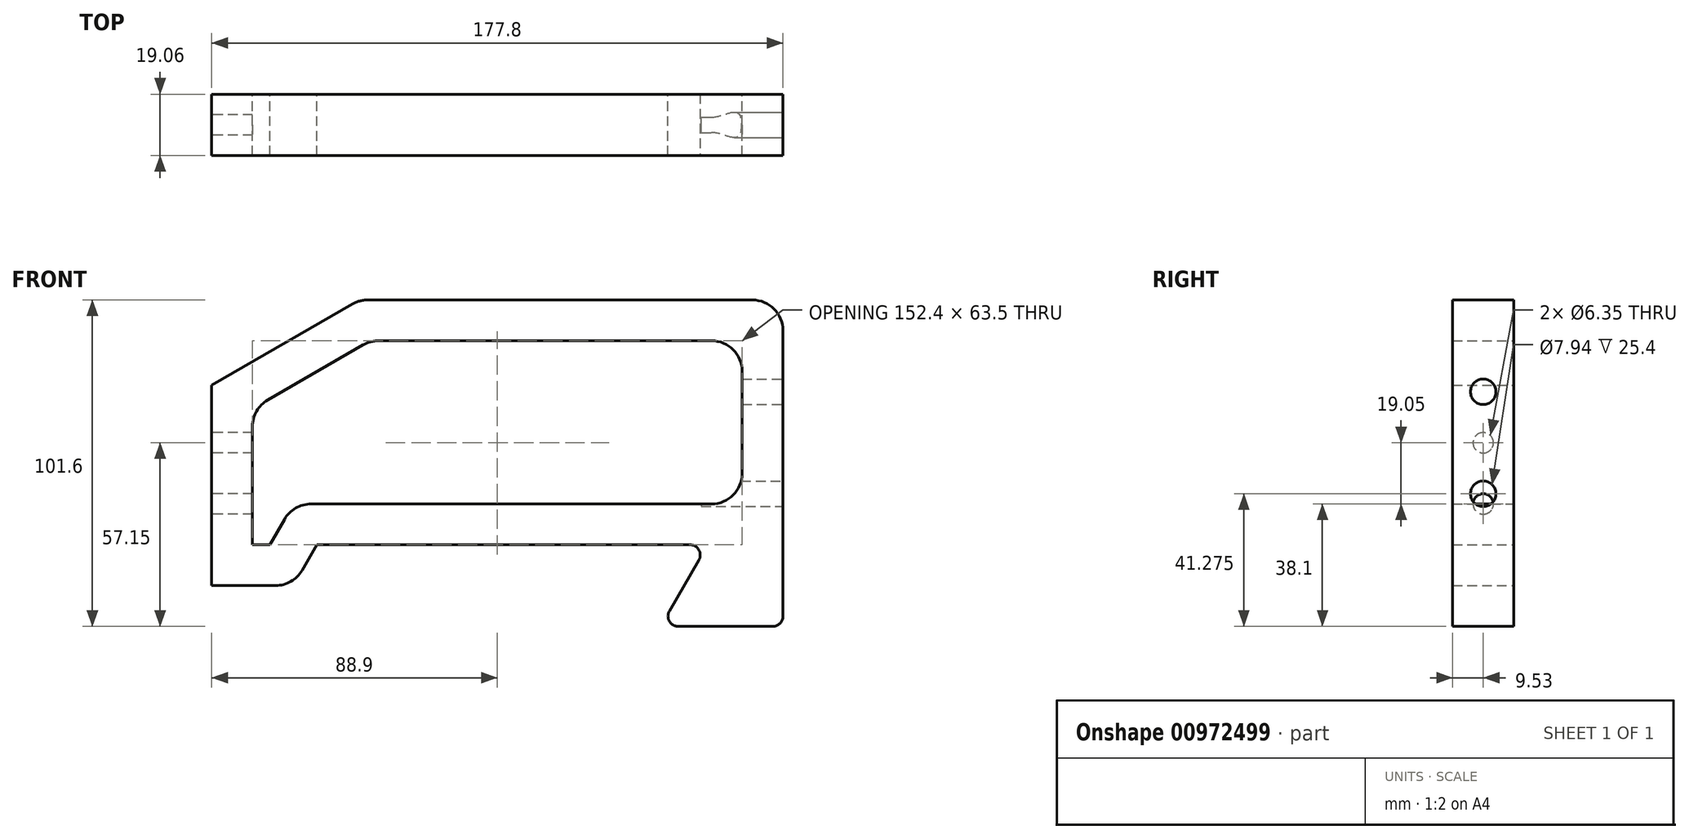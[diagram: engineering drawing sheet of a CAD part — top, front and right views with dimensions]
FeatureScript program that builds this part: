
annotation { "Feature Type Name" : "Feature", "Feature Type Description" : "" }
export const myFeature = defineFeature(function(context is Context, id is Id, definition is map)
    precondition{}
    {
        {
            var Q0;
            Q0=qCreatedBy(makeId("Front.planeOp"),FACE);
            var sketch = newSketch(context, id + "F0", { "sketchPlane" : qUnion([Q0])});
            skLineSegment(sketch, "E0", {"start": v(0, 41.2) * mm, "end": v(0, -82.16) * mm, "construction": true});
            skLineSegment(sketch, "E1", {"start": v(-50.32, 0) * mm, "end": v(100.51, 0) * mm, "construction": true});
            skLineSegment(sketch, "E2", {"start": v(-88.9, 24.27) * mm, "end": v(-88.9, -38.1) * mm});
            skLineSegment(sketch, "E3", {"start": v(-88.9, -38.1) * mm, "end": v(-63.5, -38.1) * mm});
            skLineSegment(sketch, "E4", {"start": v(-63.5, -38.1) * mm, "end": v(-56.17, -25.4) * mm});
            skLineSegment(sketch, "E5", {"start": v(-56.17, -25.4) * mm, "end": v(65.46, -25.4) * mm});
            skLineSegment(sketch, "E6", {"start": v(65.46, -25.4) * mm, "end": v(50.8, -50.8) * mm});
            skLineSegment(sketch, "E7", {"start": v(50.8, -50.8) * mm, "end": v(88.9, -50.8) * mm});
            skLineSegment(sketch, "E8", {"start": v(88.9, -50.8) * mm, "end": v(88.9, 50.8) * mm});
            skLineSegment(sketch, "E9", {"start": v(88.9, 50.8) * mm, "end": v(-42.95, 50.8) * mm});
            skLineSegment(sketch, "E10", {"start": v(-42.95, 50.8) * mm, "end": v(-88.9, 24.27) * mm});
            skLineSegment(sketch, "E11.0", {"start": v(76.2, 38.1) * mm, "end": v(-39.55, 38.1) * mm});
            skLineSegment(sketch, "E11.2", {"start": v(-39.55, 38.1) * mm, "end": v(-76.2, 16.94) * mm});
            skLineSegment(sketch, "E11.5", {"start": v(-76.2, 16.94) * mm, "end": v(-76.2, -25.4) * mm});
            skLineSegment(sketch, "E11.6", {"start": v(-76.2, -25.4) * mm, "end": v(-70.83, -25.4) * mm});
            skLineSegment(sketch, "E11.7", {"start": v(-70.83, -25.4) * mm, "end": v(-63.5, -12.7) * mm});
            skLineSegment(sketch, "E11.8", {"start": v(-63.5, -12.7) * mm, "end": v(76.2, -12.7) * mm});
            skLineSegment(sketch, "E12.trimOffspring", {"start": v(76.2, -12.7) * mm, "end": v(76.2, 38.1) * mm});
            skSolve(sketch);
        }
        {
            var Q0;
            Q0=makeQuery(id+"F0.imprint","IMPRINT",FACE,{"disambiguationData":[TD([[makeQuery(id+"F0.imprint","IMPRINT",EDGE,{"derivedFrom":sQuery(id+"F0.wireOp",EDGE,"E2")}),1.0]])]});
            extrude(context, id + "F1", {"entities" : qUnion([Q0]), "depth" : 9.52 * mm, "offsetDistance" : 25.4 * mm, "hasSecondDirection" : true, "secondDirectionOppositeDirection" : true, "secondDirectionDepth" : 9.52 * mm});
        }
        {
            var Q0;
            Q0=makeQuery(id+"F1.opExtrude","SWEPT_EDGE",EDGE,{"disambiguationData":[OSD([sQuery(id+"F0.wireOp",EDGE,"E8"),sQuery(id+"F0.wireOp",EDGE,"E9")])]});
            var Q1;
            Q1=makeQuery(id+"F1.opExtrude","SWEPT_EDGE",EDGE,{"disambiguationData":[OSD([sQuery(id+"F0.wireOp",EDGE,"E9"),sQuery(id+"F0.wireOp",EDGE,"E10")])]});
            var Q2;
            Q2=makeQuery(id+"F1.opExtrude","SWEPT_EDGE",EDGE,{"disambiguationData":[OSD([sQuery(id+"F0.wireOp",EDGE,"E3"),sQuery(id+"F0.wireOp",EDGE,"E4")])]});
            var Q3;
            Q3=makeQuery(id+"F1.opExtrude","SWEPT_EDGE",EDGE,{"disambiguationData":[OSD([sQuery(id+"F0.wireOp",EDGE,"E11.2"),sQuery(id+"F0.wireOp",EDGE,"E11.5")])]});
            var Q4;
            Q4=makeQuery(id+"F1.opExtrude","SWEPT_EDGE",EDGE,{"disambiguationData":[OSD([sQuery(id+"F0.wireOp",EDGE,"E11.0"),sQuery(id+"F0.wireOp",EDGE,"E11.2")])]});
            var Q5;
            Q5=makeQuery(id+"F1.opExtrude","SWEPT_EDGE",EDGE,{"disambiguationData":[OSD([sQuery(id+"F0.wireOp",EDGE,"E11.0"),sQuery(id+"F0.wireOp",EDGE,"E12.trimOffspring")])]});
            var Q6;
            Q6=makeQuery(id+"F1.opExtrude","SWEPT_EDGE",EDGE,{"disambiguationData":[OSD([sQuery(id+"F0.wireOp",EDGE,"E11.7"),sQuery(id+"F0.wireOp",EDGE,"E11.8")])]});
            var Q7;
            Q7=makeQuery(id+"F1.opExtrude","SWEPT_EDGE",EDGE,{"disambiguationData":[OSD([sQuery(id+"F0.wireOp",EDGE,"E11.8"),sQuery(id+"F0.wireOp",EDGE,"E12.trimOffspring")])]});
            fillet(context, id + "F2", {"entities" : qUnion([Q0, Q1, Q2, Q3, Q4, Q5, Q6, Q7]), "radius" : 9.52 * mm, "tangentPropagation" : true, "allowEdgeOverflow" : false});
        }
        {
            var Q0;
            Q0=makeQuery(id+"F1.opExtrude","SWEPT_EDGE",EDGE,{"disambiguationData":[OSD([sQuery(id+"F0.wireOp",EDGE,"E6"),sQuery(id+"F0.wireOp",EDGE,"E7")])]});
            var Q1;
            Q1=makeQuery(id+"F1.opExtrude","SWEPT_EDGE",EDGE,{"disambiguationData":[OSD([sQuery(id+"F0.wireOp",EDGE,"E5"),sQuery(id+"F0.wireOp",EDGE,"E6")])]});
            var Q2;
            Q2=makeQuery(id+"F1.opExtrude","SWEPT_EDGE",EDGE,{"disambiguationData":[OSD([sQuery(id+"F0.wireOp",EDGE,"E7"),sQuery(id+"F0.wireOp",EDGE,"E8")])]});
            fillet(context, id + "F3", {"entities" : qUnion([Q0, Q1, Q2]), "radius" : 3.17 * mm, "tangentPropagation" : true, "allowEdgeOverflow" : false});
        }
        {
            var Q0;
            Q0=makeQuery(id+"F1.opExtrude","SWEPT_FACE",FACE,{"disambiguationData":[OSD([sQuery(id+"F0.wireOp",EDGE,"E2")])]});
            var sketch = newSketch(context, id + "F4", { "sketchPlane" : qUnion([Q0])});
            skLineSegment(sketch, "E13", {"start": v(0, 22.3) * mm, "end": v(0, -38.1) * mm, "construction": true});
            skPoint(sketch, "E13.startSnap0", {"position": v(0, 24.27) * mm});
            skCircle(sketch, "E14", {"center": v(0, 6.35) * mm, "radius": 3.18 * mm});
            skCircle(sketch, "E15", {"center": v(0, -12.7) * mm, "radius": 3.18 * mm});
            skLineSegment(sketch, "E16", {"start": v(-36.09, 0) * mm, "end": v(31.9, 0) * mm, "construction": true});
            skSolve(sketch);
        }
        {
            var Q0;
            Q0=makeQuery(id+"F4.imprint","IMPRINT",FACE,{"disambiguationData":[TD([[makeQuery(id+"F4.imprint","IMPRINT",EDGE,{"derivedFrom":sQuery(id+"F4.wireOp",EDGE,"E15")}),1.0]])]});
            var Q1;
            Q1=makeQuery(id+"F4.imprint","IMPRINT",FACE,{"disambiguationData":[TD([[makeQuery(id+"F4.imprint","IMPRINT",EDGE,{"derivedFrom":sQuery(id+"F4.wireOp",EDGE,"E14")}),1.0]])]});
            var Q2;
            Q2=makeQuery(id+"F1.opExtrude","SWEPT_FACE",FACE,{"disambiguationData":[OSD([sQuery(id+"F0.wireOp",EDGE,"E11.5")])]});
            extrude(context, id + "F5", {"entities" : qUnion([Q0, Q1]), "operationType" : NewBodyOperationType.REMOVE, "endBound" : BoundingType.UP_TO_SURFACE, "oppositeDirection" : true, "depth" : 25.4 * mm, "endBoundEntityFace" : qUnion([Q2]), "offsetDistance" : 25.4 * mm});
        }
        {
            var Q0;
            Q0=makeQuery(id+"F1.opExtrude","SWEPT_FACE",FACE,{"disambiguationData":[OSD([sQuery(id+"F0.wireOp",EDGE,"E8")])]});
            var sketch = newSketch(context, id + "F6", { "sketchPlane" : qUnion([Q0])});
            skLineSegment(sketch, "E17", {"start": v(0, 57.6) * mm, "end": v(0, -68.2) * mm, "construction": true});
            skPoint(sketch, "E17.endSnap0", {"position": v(0, -47.63) * mm});
            skCircle(sketch, "E18", {"center": v(0, 22.23) * mm, "radius": 3.97 * mm});
            skCircle(sketch, "E19", {"center": v(0, -9.53) * mm, "radius": 3.97 * mm});
            skLineSegment(sketch, "E20.0", {"start": v(1.59, 57.6) * mm, "end": v(1.59, -68.2) * mm});
            skSolve(sketch);
        }
        {
            var Q0;
            {var subQ0=sQuery(id+"F6.wireOp",EDGE,"E20.0");var subQ1=sQuery(id+"F6.wireOp",EDGE,"E19");var subQ2=makeQuery(id+"F6.imprint","INTERSECT",VERTEX,{"disambiguationData":[OD(0.0)],"derivedFrom":[subQ1,subQ0]});Q0=makeQuery(id+"F6.imprint","IMPRINT",FACE,{"disambiguationData":[TD([[makeQuery(id+"F6.imprint","IMPRINT",EDGE,{"disambiguationData":[TD([[subQ2,1.0]])],"derivedFrom":subQ1}),1.0]])]});}
            var Q1;
            {var subQ0=sQuery(id+"F6.wireOp",EDGE,"E20.0");var subQ1=sQuery(id+"F6.wireOp",EDGE,"E19");var subQ2=makeQuery(id+"F6.imprint","INTERSECT",VERTEX,{"disambiguationData":[OD(0.0)],"derivedFrom":[subQ1,subQ0]});Q1=makeQuery(id+"F6.imprint","IMPRINT",FACE,{"disambiguationData":[TD([[makeQuery(id+"F6.imprint","IMPRINT",EDGE,{"disambiguationData":[TD([[subQ2,-1.0]])],"derivedFrom":subQ1}),1.0]])]});}
            var Q2;
            {var subQ0=sQuery(id+"F6.wireOp",EDGE,"E20.0");var subQ1=sQuery(id+"F6.wireOp",EDGE,"E18");var subQ2=makeQuery(id+"F6.imprint","INTERSECT",VERTEX,{"disambiguationData":[OD(0.0)],"derivedFrom":[subQ1,subQ0]});Q2=makeQuery(id+"F6.imprint","IMPRINT",FACE,{"disambiguationData":[TD([[makeQuery(id+"F6.imprint","IMPRINT",EDGE,{"disambiguationData":[TD([[subQ2,-1.0]])],"derivedFrom":subQ1}),1.0]])]});}
            var Q3;
            {var subQ0=sQuery(id+"F6.wireOp",EDGE,"E20.0");var subQ1=sQuery(id+"F6.wireOp",EDGE,"E18");var subQ2=makeQuery(id+"F6.imprint","INTERSECT",VERTEX,{"disambiguationData":[OD(0.0)],"derivedFrom":[subQ1,subQ0]});Q3=makeQuery(id+"F6.imprint","IMPRINT",FACE,{"disambiguationData":[TD([[makeQuery(id+"F6.imprint","IMPRINT",EDGE,{"disambiguationData":[TD([[subQ2,1.0]])],"derivedFrom":subQ1}),1.0]])]});}
            extrude(context, id + "F7", {"entities" : qUnion([Q0, Q1, Q2, Q3]), "operationType" : NewBodyOperationType.REMOVE, "oppositeDirection" : true, "depth" : 25.4 * mm, "offsetDistance" : 25.4 * mm});
        }
    });
